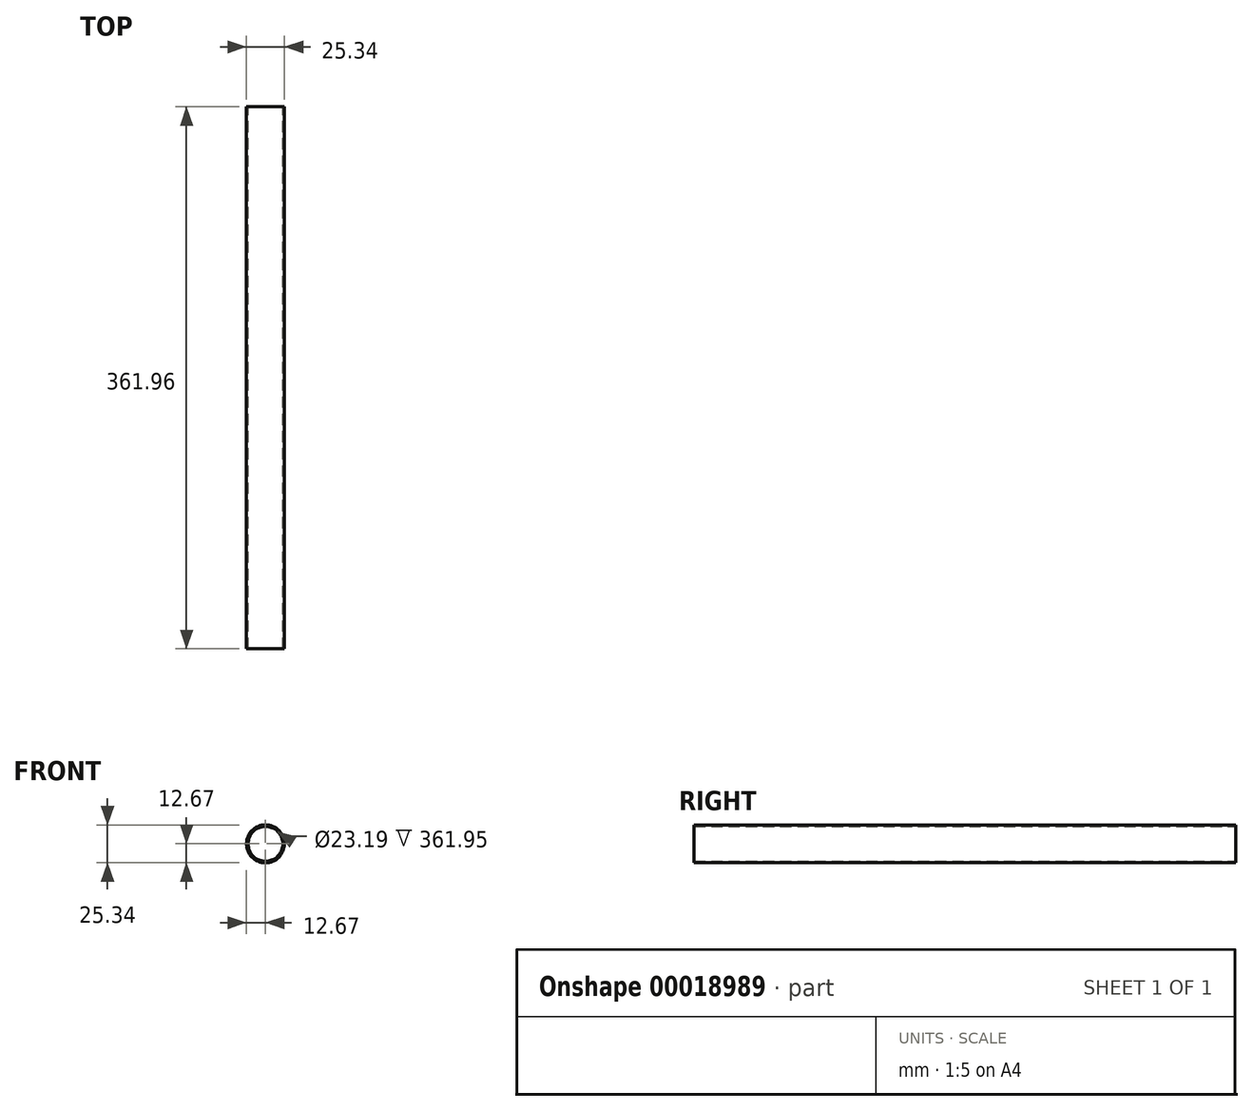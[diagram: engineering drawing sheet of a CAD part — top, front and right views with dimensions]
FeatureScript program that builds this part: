
annotation { "Feature Type Name" : "Feature", "Feature Type Description" : "" }
export const myFeature = defineFeature(function(context is Context, id is Id, definition is map)
    precondition{}
    {
        {
            var Q0;
            Q0=qCreatedBy(makeId("Front.planeOp"),FACE);
            var sketch = newSketch(context, id + "F0", { "sketchPlane" : qUnion([Q0])});
            skCircle(sketch, "E0", {"center": v(0, 0) * mm, "radius": 12.67 * mm});
            skCircle(sketch, "E1", {"center": v(0, 0) * mm, "radius": 11.6 * mm});
            skSolve(sketch);
        }
        {
            var Q0;
            Q0 = qSketchRegion(id + "F0", true);
            extrude(context, id + "F1", {"entities" : qUnion([Q0]), "endBound" : BoundingType.SYMMETRIC, "depth" : 361.95 * mm});
        }
    });
